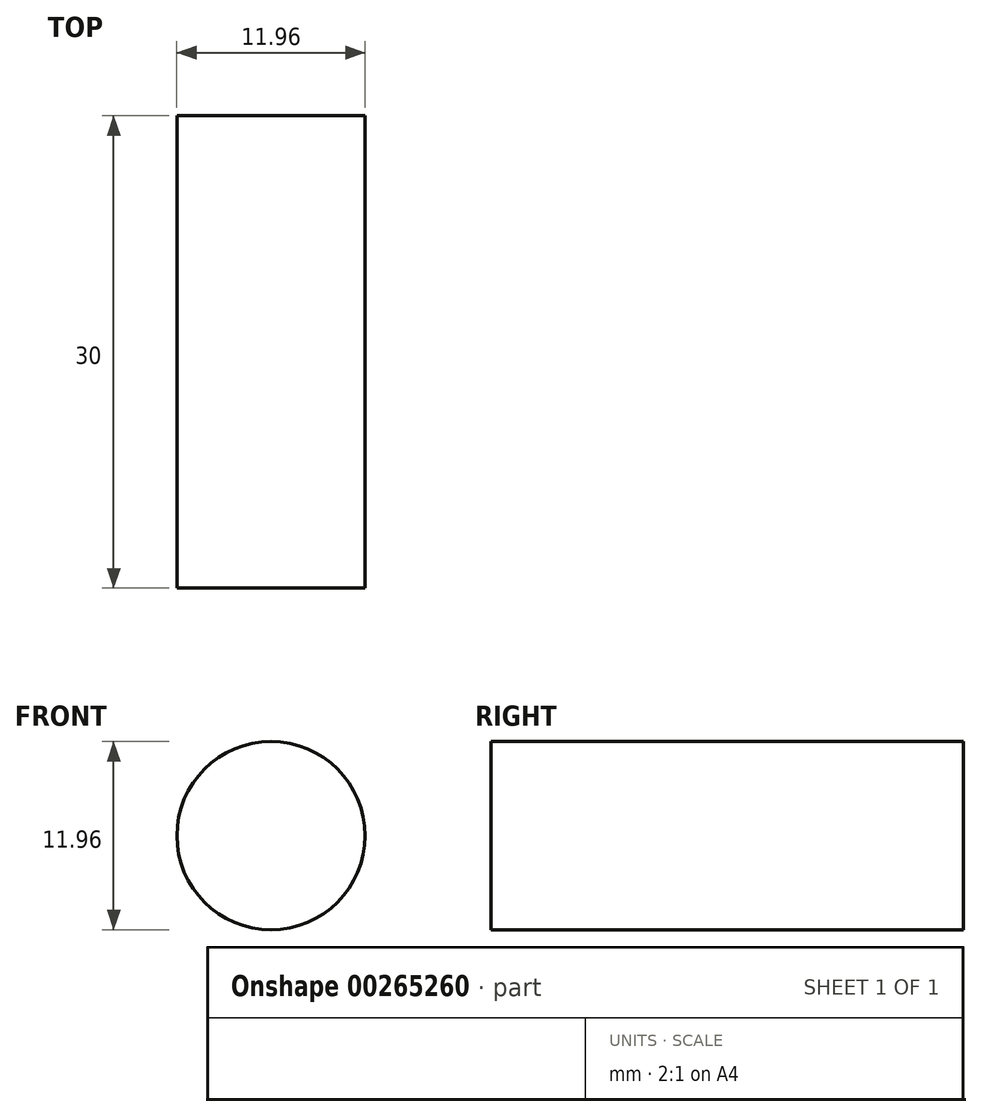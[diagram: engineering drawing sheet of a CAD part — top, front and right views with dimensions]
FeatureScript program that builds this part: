
annotation { "Feature Type Name" : "Feature", "Feature Type Description" : "" }
export const myFeature = defineFeature(function(context is Context, id is Id, definition is map)
    precondition{}
    {
        {
            var Q0;
            Q0=qCreatedBy(makeId("Front.planeOp"),FACE);
            var sketch = newSketch(context, id + "F0", { "sketchPlane" : qUnion([Q0])});
            skCircle(sketch, "E0", {"center": v(0, 0) * mm, "radius": 5.97 * mm});
            skSolve(sketch);
        }
        {
            var Q0;
            Q0 = qSketchRegion(id + "F0", true);
            extrude(context, id + "F1", {"entities" : qUnion([Q0]), "depth" : 30 * mm});
        }
    });
